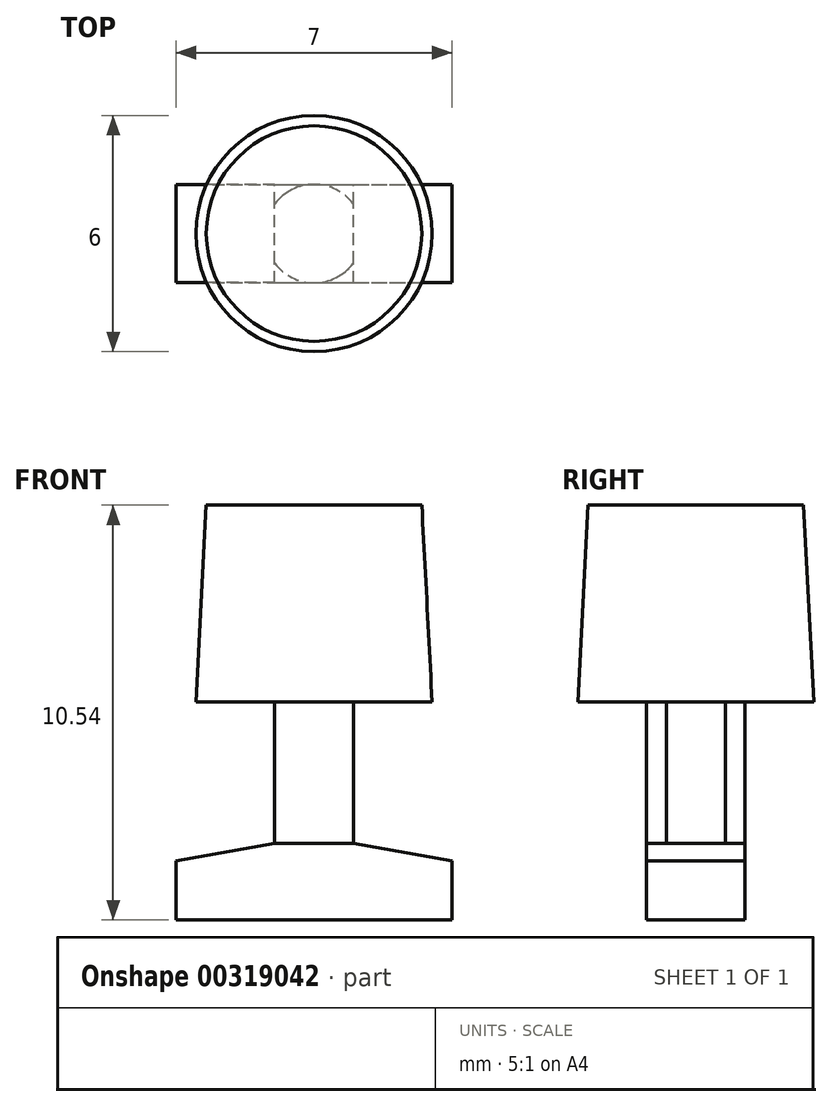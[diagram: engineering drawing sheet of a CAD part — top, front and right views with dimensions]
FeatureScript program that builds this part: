
annotation { "Feature Type Name" : "Feature", "Feature Type Description" : "" }
export const myFeature = defineFeature(function(context is Context, id is Id, definition is map)
    precondition{}
    {
        {
            var Q0;
            Q0=qCreatedBy(makeId("Front.planeOp"),FACE);
            var sketch = newSketch(context, id + "F0", { "sketchPlane" : qUnion([Q0])});
            skLineSegment(sketch, "E0", {"start": v(1, 0.97) * mm, "end": v(3.5, 0.53) * mm});
            skLineSegment(sketch, "E1", {"start": v(3.5, 0.53) * mm, "end": v(3.5, -0.97) * mm});
            skLineSegment(sketch, "E2", {"start": v(0, 0.97) * mm, "end": v(0, -0.97) * mm, "construction": true});
            skLineSegment(sketch, "E3", {"start": v(3.5, -0.97) * mm, "end": v(0, -0.97) * mm});
            skLineSegment(sketch, "E4.MirrorCS", {"start": v(-3.5, -0.97) * mm, "end": v(0, -0.97) * mm});
            skLineSegment(sketch, "E5.MirrorCS", {"start": v(-1, 0.97) * mm, "end": v(-3.5, 0.53) * mm});
            skLineSegment(sketch, "E6.MirrorCS", {"start": v(-3.5, 0.53) * mm, "end": v(-3.5, -0.97) * mm});
            skLineSegment(sketch, "E7", {"start": v(-1, 0.97) * mm, "end": v(1, 0.97) * mm});
            skPoint(sketch, "E8", {"position": v(0, 0) * mm});
            skSolve(sketch);
        }
        {
            var Q0;
            Q0=makeQuery(id+"F0.imprint","IMPRINT",FACE,{"disambiguationData":[TD([[makeQuery(id+"F0.imprint","IMPRINT",EDGE,{"derivedFrom":sQuery(id+"F0.wireOp",EDGE,"E0")}),-1.0]])]});
            extrude(context, id + "F1", {"entities" : qUnion([Q0]), "endBound" : BoundingType.SYMMETRIC, "depth" : 2.5 * mm});
        }
        {
            var Q0;
            Q0=makeQuery(id+"F1.opExtrude","SWEPT_FACE",FACE,{"disambiguationData":[OSD([sQuery(id+"F0.wireOp",EDGE,"E7")])]});
            var sketch = newSketch(context, id + "F2", { "sketchPlane" : qUnion([Q0])});
            skCircle(sketch, "E9", {"center": v(0, 0) * mm, "radius": 1.25 * mm});
            skSolve(sketch);
        }
        {
            var Q0;
            {var subQ0=sQuery(id+"F2.wireOp",EDGE,"E9");var subQ1=sQuery(id+"F0.wireOp",EDGE,"E7");var subQ7=makeQuery(id+"F2.imprint","INTERSECT",VERTEX,{"derivedFrom":[makeQuery(id+"F1.opExtrude","CAP_EDGE",EDGE,{"disambiguationData":[OSD([subQ1])],"isStart":true}),subQ0]});Q0=makeQuery(id+"F2.imprint","IMPRINT",FACE,{"disambiguationData":[TD([[makeQuery(id+"F2.imprint","IMPRINT",EDGE,{"disambiguationData":[TD([[subQ7,1.0]])],"derivedFrom":subQ0}),1.0]])]});}
            extrude(context, id + "F3", {"entities" : qUnion([Q0]), "operationType" : NewBodyOperationType.ADD, "depth" : 3.6 * mm});
        }
        {
            var Q0;
            Q0=makeQuery(id+"F3.opExtrude","CAP_FACE",FACE,{"disambiguationData":[OSD([sQuery(id+"F0.wireOp",EDGE,"E0"),sQuery(id+"F0.wireOp",EDGE,"E5.MirrorCS"),sQuery(id+"F0.wireOp",EDGE,"E7"),sQuery(id+"F2.wireOp",EDGE,"E9")])],"isStart":false});
            var sketch = newSketch(context, id + "F4", { "sketchPlane" : qUnion([Q0])});
            skCircle(sketch, "E10", {"center": v(0, 0) * mm, "radius": 3 * mm});
            skSolve(sketch);
        }
        {
            var Q0;
            Q0=makeQuery(id+"F4.imprint","IMPRINT",FACE,{"disambiguationData":[TD([[makeQuery(id+"F4.imprint","IMPRINT",EDGE,{"derivedFrom":sQuery(id+"F4.wireOp",EDGE,"E10")}),1.0]])]});
            var Q1;
            {var subQ1=sQuery(id+"F0.wireOp",EDGE,"E7");var subQ5=sQuery(id+"F0.wireOp",EDGE,"E0");Q1=makeQuery(id+"F4.imprint","IMPRINT",FACE,{"disambiguationData":[TD([[makeQuery(id+"F4.imprint","IMPRINT",EDGE,{"derivedFrom":makeQuery(id+"F3.opExtrude","CAP_EDGE",EDGE,{"disambiguationData":[OSD([subQ5,subQ1])],"isStart":false})}),1.0]])]});}
            extrude(context, id + "F5", {"entities" : qUnion([Q0, Q1]), "operationType" : NewBodyOperationType.ADD, "depth" : 5 * mm, "hasDraft" : true, "draftAngle" : 3 * degree, "draftPullDirection" : true});
        }
    });
